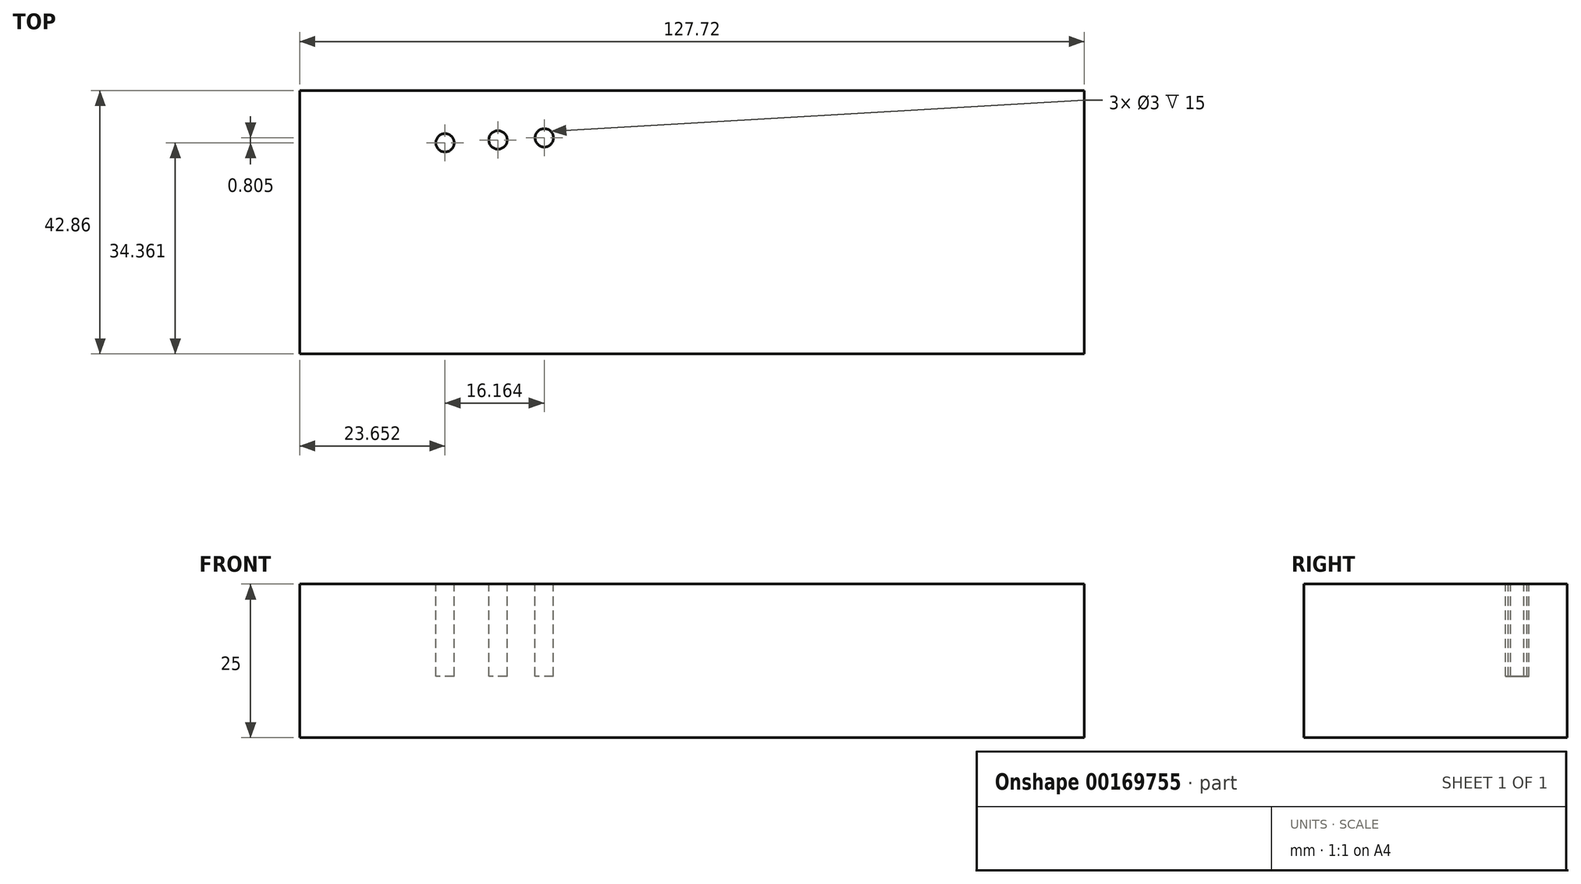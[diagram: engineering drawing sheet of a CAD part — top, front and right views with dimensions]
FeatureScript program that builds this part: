
annotation { "Feature Type Name" : "Feature", "Feature Type Description" : "" }
export const myFeature = defineFeature(function(context is Context, id is Id, definition is map)
    precondition{}
    {
        {
            var Q0;
            Q0=qCreatedBy(makeId("Top.planeOp"),FACE);
            var sketch = newSketch(context, id + "F0", { "sketchPlane" : qUnion([Q0])});
            skLineSegment(sketch, "E0.rect.bottom", {"start": v(-63.86, -21.43) * mm, "end": v(63.86, -21.43) * mm});
            skLineSegment(sketch, "E0.rect.top", {"start": v(-63.86, 21.43) * mm, "end": v(63.86, 21.43) * mm});
            skLineSegment(sketch, "E0.rect.left", {"start": v(-63.86, -21.43) * mm, "end": v(-63.86, 21.43) * mm});
            skLineSegment(sketch, "E0.rect.right", {"start": v(63.86, -21.43) * mm, "end": v(63.86, 21.43) * mm});
            skPoint(sketch, "E0.rect.middle", {"position": v(0, 0) * mm});
            skSolve(sketch);
        }
        {
            var Q0;
            Q0=qSketchRegion(id+"F0",true);
            extrude(context, id + "F1", {"entities" : qUnion([Q0]), "depth" : 25 * mm});
        }
        {
            var Q0;
            Q0=makeQuery(id+"F1.opExtrude","CAP_FACE",FACE,{"disambiguationData":[OSD([sQuery(id+"F0.wireOp",EDGE,"E0.rect.bottom"),sQuery(id+"F0.wireOp",EDGE,"E0.rect.top"),sQuery(id+"F0.wireOp",EDGE,"E0.rect.left"),sQuery(id+"F0.wireOp",EDGE,"E0.rect.right")])],"isStart":false});
            var sketch = newSketch(context, id + "F2", { "sketchPlane" : qUnion([Q0])});
            skCircle(sketch, "E1", {"center": v(-40.2, 12.93) * mm, "radius": 1.5 * mm});
            skCircle(sketch, "E2", {"center": v(-31.58, 13.4) * mm, "radius": 1.5 * mm});
            skCircle(sketch, "E3", {"center": v(-24.04, 13.74) * mm, "radius": 1.5 * mm});
            skSolve(sketch);
        }
        {
            var Q0;
            Q0=qSketchRegion(id+"F2",true);
            extrude(context, id + "F3", {"entities" : qUnion([Q0]), "operationType" : NewBodyOperationType.REMOVE, "oppositeDirection" : true, "depth" : 15 * mm});
        }
    });
